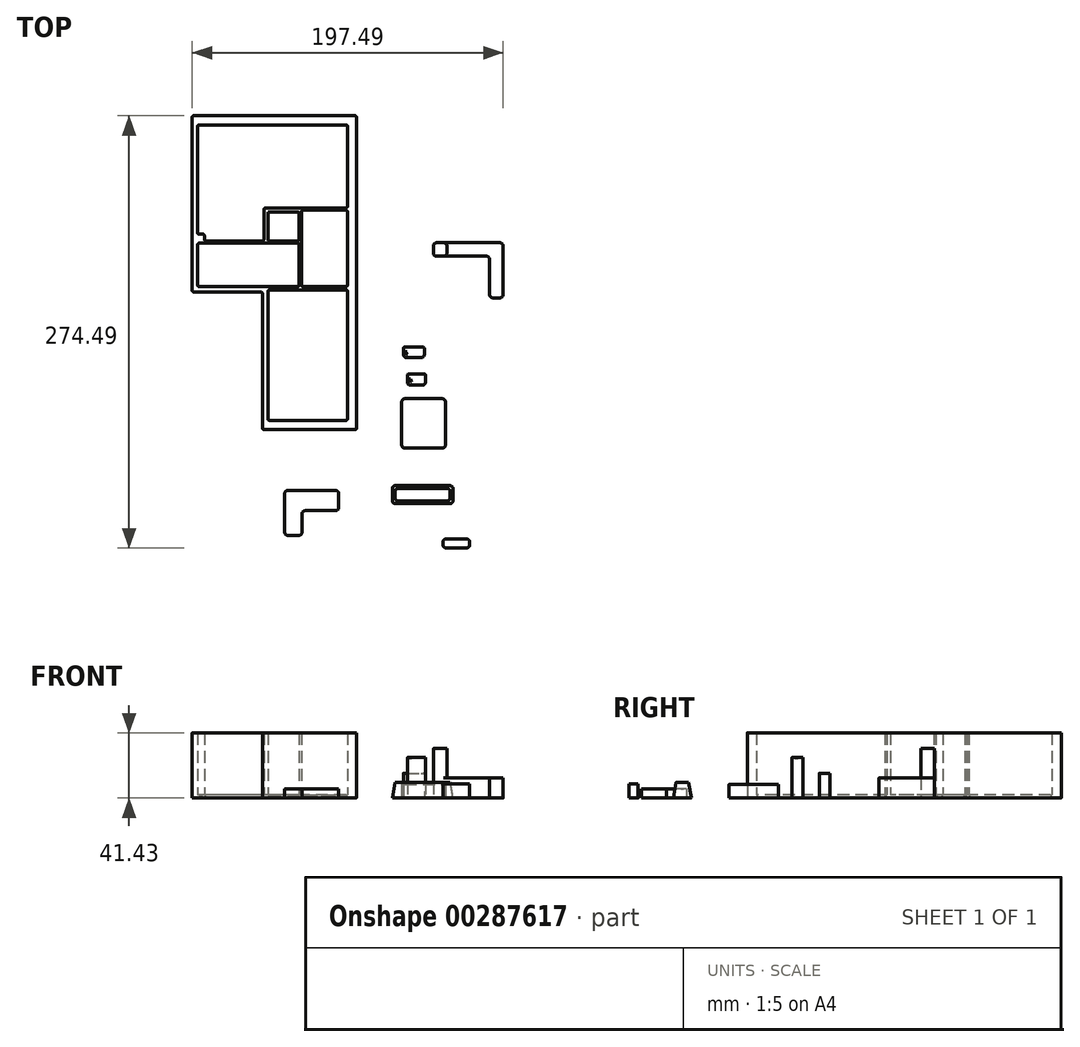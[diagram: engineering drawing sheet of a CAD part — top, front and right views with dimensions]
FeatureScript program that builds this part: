
annotation { "Feature Type Name" : "Feature", "Feature Type Description" : "" }
export const myFeature = defineFeature(function(context is Context, id is Id, definition is map)
    precondition{}
    {
        {
            assignVariable(context, id + "F0", {"name" : "Scale", "anyValue" : 1 / 7});
        }
        {
            var Q0;
            Q0=qCreatedBy(makeId("Top.planeOp"),FACE);
            var sketch = newSketch(context, id + "F1", { "sketchPlane" : qUnion([Q0])});
            skLineSegment(sketch, "E0", {"start": v(0, 0) * mm, "end": v(-59.71, 0) * mm});
            skLineSegment(sketch, "E1", {"start": v(-59.71, 0) * mm, "end": v(-59.71, 87.43) * mm});
            skLineSegment(sketch, "E2", {"start": v(0, 199.36) * mm, "end": v(-104.36, 199.36) * mm});
            skLineSegment(sketch, "E3", {"start": v(0, 0) * mm, "end": v(0, 199.36) * mm});
            skLineSegment(sketch, "E4", {"start": v(-104.36, 199.36) * mm, "end": v(-104.36, 87.43) * mm});
            skLineSegment(sketch, "E5", {"start": v(-104.36, 87.43) * mm, "end": v(-59.71, 87.43) * mm});
            skLineSegment(sketch, "E6", {"start": v(-5.71, 199.36) * mm, "end": v(-5.71, 0) * mm});
            skLineSegment(sketch, "E7", {"start": v(0, 193.5) * mm, "end": v(-104.36, 193.5) * mm});
            skLineSegment(sketch, "E8", {"start": v(-100.93, 199.36) * mm, "end": v(-100.93, 87.43) * mm});
            skLineSegment(sketch, "E9", {"start": v(-56.29, 0) * mm, "end": v(-56.29, 90.86) * mm});
            skLineSegment(sketch, "E10", {"start": v(-56.29, 90.86) * mm, "end": v(-104.36, 90.86) * mm});
            skLineSegment(sketch, "E11", {"start": v(-59.71, 5.86) * mm, "end": v(0, 5.86) * mm});
            skLineSegment(sketch, "E12", {"start": v(-56.29, 90.86) * mm, "end": v(-5.71, 90.86) * mm});
            skLineSegment(sketch, "E13", {"start": v(-34.97, 90.86) * mm, "end": v(-34.97, 139.36) * mm});
            skLineSegment(sketch, "E14", {"start": v(-34.97, 139.36) * mm, "end": v(-5.71, 139.36) * mm});
            skLineSegment(sketch, "E15", {"start": v(-5.71, 140.79) * mm, "end": v(-36.4, 140.79) * mm});
            skLineSegment(sketch, "E16", {"start": v(-36.4, 140.79) * mm, "end": v(-36.4, 90.86) * mm});
            skLineSegment(sketch, "E17", {"start": v(-36.4, 138.29) * mm, "end": v(-56.3, 138.29) * mm});
            skLineSegment(sketch, "E18", {"start": v(-36.4, 140.79) * mm, "end": v(-58.8, 140.79) * mm});
            skLineSegment(sketch, "E19", {"start": v(-58.8, 140.79) * mm, "end": v(-58.8, 119.87) * mm});
            skLineSegment(sketch, "E20", {"start": v(-58.8, 119.87) * mm, "end": v(-36.4, 119.87) * mm});
            skLineSegment(sketch, "E21", {"start": v(-56.3, 138.29) * mm, "end": v(-56.3, 119.87) * mm});
            skLineSegment(sketch, "E22", {"start": v(-36.4, 118.44) * mm, "end": v(-58.8, 118.44) * mm});
            skLineSegment(sketch, "E23", {"start": v(-58.8, 118.44) * mm, "end": v(-58.8, 119.87) * mm});
            skLineSegment(sketch, "E24", {"start": v(-5.71, 88.71) * mm, "end": v(-56.29, 88.71) * mm});
            skLineSegment(sketch, "E25", {"start": v(-56.29, 88.71) * mm, "end": v(-56.29, 90.86) * mm});
            skLineSegment(sketch, "E26", {"start": v(-58.8, 118.44) * mm, "end": v(-100.93, 118.44) * mm});
            skLineSegment(sketch, "E27", {"start": v(-58.8, 119.87) * mm, "end": v(-100.93, 119.87) * mm});
            skLineSegment(sketch, "E28", {"start": v(-100.93, 124.16) * mm, "end": v(-96.64, 124.16) * mm});
            skLineSegment(sketch, "E29", {"start": v(-96.64, 124.16) * mm, "end": v(-96.64, 119.87) * mm});
            skSolve(sketch);
        }
        {
            var Q0;
            Q0 = qSketchRegion(id + "F1", true);
            var Q1;
            {var subQ1=sQuery(id+"F1.wireOp",EDGE,"E17");Q1=makeQuery(id+"F1.imprint","IMPRINT",FACE,{"disambiguationData":[TD([[makeQuery(id+"F1.imprint","IMPRINT",EDGE,{"derivedFrom":subQ1}),-1.0]])]});}
            var Q2;
            {var subQ0=sQuery(id+"F1.wireOp",EDGE,"E13");Q2=makeQuery(id+"F1.imprint","IMPRINT",FACE,{"disambiguationData":[TD([[makeQuery(id+"F1.imprint","IMPRINT",EDGE,{"derivedFrom":subQ0}),1.0]])]});}
            var Q3;
            {var subQ6=sQuery(id+"F1.wireOp",EDGE,"E24");Q3=makeQuery(id+"F1.imprint","IMPRINT",FACE,{"disambiguationData":[TD([[makeQuery(id+"F1.imprint","IMPRINT",EDGE,{"derivedFrom":subQ6}),-1.0]])]});}
            var Q4;
            {var subQ0=sQuery(id+"F1.wireOp",EDGE,"E22");Q4=makeQuery(id+"F1.imprint","IMPRINT",FACE,{"disambiguationData":[TD([[makeQuery(id+"F1.imprint","IMPRINT",EDGE,{"derivedFrom":subQ0}),-1.0]])]});}
            var Q5;
            {var subQ3=sQuery(id+"F1.wireOp",EDGE,"E28");Q5=makeQuery(id+"F1.imprint","IMPRINT",FACE,{"disambiguationData":[TD([[makeQuery(id+"F1.imprint","IMPRINT",EDGE,{"derivedFrom":subQ3}),-1.0]])]});}
            var Q6;
            {var subQ1=sQuery(id+"F1.wireOp",EDGE,"E23");Q6=makeQuery(id+"F1.imprint","IMPRINT",FACE,{"disambiguationData":[TD([[makeQuery(id+"F1.imprint","IMPRINT",EDGE,{"derivedFrom":subQ1}),1.0]])]});}
            extrude(context, id + "F2", {"entities" : qUnion([Q0, Q1, Q2, Q3, Q4, Q5, Q6]), "depth" : (290 * getVariable(context, 'Scale')) * mm});
        }
        {
            var Q0;
            Q0 = qSketchRegion(id + "F1", true);
            var Q1;
            {var subQ0=sQuery(id+"F1.wireOp",EDGE,"E15");Q1=makeQuery(id+"F1.imprint","IMPRINT",FACE,{"disambiguationData":[TD([[makeQuery(id+"F1.imprint","IMPRINT",EDGE,{"derivedFrom":subQ0}),-1.0]])]});}
            var Q2;
            {var subQ1=sQuery(id+"F1.wireOp",EDGE,"E17");Q2=makeQuery(id+"F1.imprint","IMPRINT",FACE,{"disambiguationData":[TD([[makeQuery(id+"F1.imprint","IMPRINT",EDGE,{"derivedFrom":subQ1}),-1.0]])]});}
            var Q3;
            {var subQ4=sQuery(id+"F1.wireOp",EDGE,"E13");Q3=makeQuery(id+"F1.imprint","IMPRINT",FACE,{"disambiguationData":[TD([[makeQuery(id+"F1.imprint","IMPRINT",EDGE,{"derivedFrom":subQ4}),-1.0]])]});}
            var Q4;
            {var subQ3=sQuery(id+"F1.wireOp",EDGE,"E22");Q4=makeQuery(id+"F1.imprint","IMPRINT",FACE,{"disambiguationData":[TD([[makeQuery(id+"F1.imprint","IMPRINT",EDGE,{"derivedFrom":subQ3}),1.0]])]});}
            var Q5;
            {var subQ0=sQuery(id+"F1.wireOp",EDGE,"E17");Q5=makeQuery(id+"F1.imprint","IMPRINT",FACE,{"disambiguationData":[TD([[makeQuery(id+"F1.imprint","IMPRINT",EDGE,{"derivedFrom":subQ0}),1.0]])]});}
            var Q6;
            {var subQ0=sQuery(id+"F1.wireOp",EDGE,"E24");Q6=makeQuery(id+"F1.imprint","IMPRINT",FACE,{"disambiguationData":[TD([[makeQuery(id+"F1.imprint","IMPRINT",EDGE,{"derivedFrom":subQ0}),1.0]])]});}
            var Q7;
            {var subQ6=sQuery(id+"F1.wireOp",EDGE,"E24");Q7=makeQuery(id+"F1.imprint","IMPRINT",FACE,{"disambiguationData":[TD([[makeQuery(id+"F1.imprint","IMPRINT",EDGE,{"derivedFrom":subQ6}),-1.0]])]});}
            var Q8;
            {var subQ0=sQuery(id+"F1.wireOp",EDGE,"E13");Q8=makeQuery(id+"F1.imprint","IMPRINT",FACE,{"disambiguationData":[TD([[makeQuery(id+"F1.imprint","IMPRINT",EDGE,{"derivedFrom":subQ0}),1.0]])]});}
            var Q9;
            {var subQ0=sQuery(id+"F1.wireOp",EDGE,"E22");Q9=makeQuery(id+"F1.imprint","IMPRINT",FACE,{"disambiguationData":[TD([[makeQuery(id+"F1.imprint","IMPRINT",EDGE,{"derivedFrom":subQ0}),-1.0]])]});}
            var Q10;
            {var subQ1=sQuery(id+"F1.wireOp",EDGE,"E23");Q10=makeQuery(id+"F1.imprint","IMPRINT",FACE,{"disambiguationData":[TD([[makeQuery(id+"F1.imprint","IMPRINT",EDGE,{"derivedFrom":subQ1}),1.0]])]});}
            var Q11;
            {var subQ3=sQuery(id+"F1.wireOp",EDGE,"E28");Q11=makeQuery(id+"F1.imprint","IMPRINT",FACE,{"disambiguationData":[TD([[makeQuery(id+"F1.imprint","IMPRINT",EDGE,{"derivedFrom":subQ3}),-1.0]])]});}
            extrude(context, id + "F3", {"entities" : qUnion([Q0, Q1, Q2, Q3, Q4, Q5, Q6, Q7, Q8, Q9, Q10, Q11]), "operationType" : NewBodyOperationType.ADD, "depth" : 2 * mm});
        }
        {
            var Q0;
            Q0=makeQuery(id+"F2.opExtrude","SWEPT_EDGE",EDGE,{"disambiguationData":[OSD([sQuery(id+"F1.wireOp",EDGE,"E7"),sQuery(id+"F1.wireOp",EDGE,"E8")])]});
            var Q1;
            Q1=makeQuery(id+"F2.opExtrude","SWEPT_EDGE",EDGE,{"disambiguationData":[OSD([sQuery(id+"F1.wireOp",EDGE,"E8"),sQuery(id+"F1.wireOp",EDGE,"E28")])]});
            var Q2;
            Q2=makeQuery(id+"F2.opExtrude","SWEPT_EDGE",EDGE,{"disambiguationData":[OSD([sQuery(id+"F1.wireOp",EDGE,"E28"),sQuery(id+"F1.wireOp",EDGE,"E29")])]});
            var Q3;
            Q3=makeQuery(id+"F2.opExtrude","SWEPT_EDGE",EDGE,{"disambiguationData":[OSD([sQuery(id+"F1.wireOp",EDGE,"E27"),sQuery(id+"F1.wireOp",EDGE,"E29")])]});
            var Q4;
            Q4=makeQuery(id+"F2.opExtrude","SWEPT_EDGE",EDGE,{"disambiguationData":[OSD([sQuery(id+"F1.wireOp",EDGE,"E19"),sQuery(id+"F1.wireOp",EDGE,"E20"),sQuery(id+"F1.wireOp",EDGE,"E23"),sQuery(id+"F1.wireOp",EDGE,"E27")])]});
            var Q5;
            Q5=makeQuery(id+"F2.opExtrude","SWEPT_EDGE",EDGE,{"disambiguationData":[OSD([sQuery(id+"F1.wireOp",EDGE,"E18"),sQuery(id+"F1.wireOp",EDGE,"E19")])]});
            var Q6;
            Q6=makeQuery(id+"F2.opExtrude","SWEPT_EDGE",EDGE,{"disambiguationData":[OSD([sQuery(id+"F1.wireOp",EDGE,"E6"),sQuery(id+"F1.wireOp",EDGE,"E15")])]});
            var Q7;
            Q7=makeQuery(id+"F2.opExtrude","SWEPT_EDGE",EDGE,{"disambiguationData":[OSD([sQuery(id+"F1.wireOp",EDGE,"E6"),sQuery(id+"F1.wireOp",EDGE,"E7")])]});
            var Q8;
            Q8=makeQuery(id+"F2.opExtrude","SWEPT_EDGE",EDGE,{"disambiguationData":[OSD([sQuery(id+"F1.wireOp",EDGE,"E16"),sQuery(id+"F1.wireOp",EDGE,"E17")])]});
            var Q9;
            Q9=makeQuery(id+"F2.opExtrude","SWEPT_EDGE",EDGE,{"disambiguationData":[OSD([sQuery(id+"F1.wireOp",EDGE,"E20"),sQuery(id+"F1.wireOp",EDGE,"E21")])]});
            var Q10;
            Q10=makeQuery(id+"F2.opExtrude","SWEPT_EDGE",EDGE,{"disambiguationData":[OSD([sQuery(id+"F1.wireOp",EDGE,"E16"),sQuery(id+"F1.wireOp",EDGE,"E20")])]});
            var Q11;
            Q11=makeQuery(id+"F2.opExtrude","SWEPT_EDGE",EDGE,{"disambiguationData":[OSD([sQuery(id+"F1.wireOp",EDGE,"E13"),sQuery(id+"F1.wireOp",EDGE,"E14")])]});
            var Q12;
            Q12=makeQuery(id+"F2.opExtrude","SWEPT_EDGE",EDGE,{"disambiguationData":[OSD([sQuery(id+"F1.wireOp",EDGE,"E6"),sQuery(id+"F1.wireOp",EDGE,"E12")])]});
            var Q13;
            Q13=makeQuery(id+"F2.opExtrude","SWEPT_EDGE",EDGE,{"disambiguationData":[OSD([sQuery(id+"F1.wireOp",EDGE,"E12"),sQuery(id+"F1.wireOp",EDGE,"E13")])]});
            var Q14;
            Q14=makeQuery(id+"F2.opExtrude","SWEPT_EDGE",EDGE,{"disambiguationData":[OSD([sQuery(id+"F1.wireOp",EDGE,"E16"),sQuery(id+"F1.wireOp",EDGE,"E22")])]});
            var Q15;
            Q15=makeQuery(id+"F2.opExtrude","SWEPT_EDGE",EDGE,{"disambiguationData":[OSD([sQuery(id+"F1.wireOp",EDGE,"E8"),sQuery(id+"F1.wireOp",EDGE,"E10")])]});
            var Q16;
            Q16=makeQuery(id+"F2.opExtrude","SWEPT_EDGE",EDGE,{"disambiguationData":[OSD([sQuery(id+"F1.wireOp",EDGE,"E12"),sQuery(id+"F1.wireOp",EDGE,"E16")])]});
            var Q17;
            Q17=makeQuery(id+"F2.opExtrude","SWEPT_EDGE",EDGE,{"disambiguationData":[OSD([sQuery(id+"F1.wireOp",EDGE,"E6"),sQuery(id+"F1.wireOp",EDGE,"E24")])]});
            var Q18;
            Q18=makeQuery(id+"F2.opExtrude","SWEPT_EDGE",EDGE,{"disambiguationData":[OSD([sQuery(id+"F1.wireOp",EDGE,"E9"),sQuery(id+"F1.wireOp",EDGE,"E24"),sQuery(id+"F1.wireOp",EDGE,"E25")])]});
            var Q19;
            Q19=makeQuery(id+"F2.opExtrude","SWEPT_EDGE",EDGE,{"disambiguationData":[OSD([sQuery(id+"F1.wireOp",EDGE,"E9"),sQuery(id+"F1.wireOp",EDGE,"E11")])]});
            var Q20;
            Q20=makeQuery(id+"F2.opExtrude","SWEPT_EDGE",EDGE,{"disambiguationData":[OSD([sQuery(id+"F1.wireOp",EDGE,"E6"),sQuery(id+"F1.wireOp",EDGE,"E11")])]});
            var Q21;
            Q21=makeQuery(id+"F2.opExtrude","SWEPT_EDGE",EDGE,{"disambiguationData":[OSD([sQuery(id+"F1.wireOp",EDGE,"E6"),sQuery(id+"F1.wireOp",EDGE,"E14")])]});
            var Q22;
            Q22=makeQuery(id+"F2.opExtrude","SWEPT_EDGE",EDGE,{"disambiguationData":[OSD([sQuery(id+"F1.wireOp",EDGE,"E8"),sQuery(id+"F1.wireOp",EDGE,"E26")])]});
            fillet(context, id + "F4", {"entities" : qUnion([Q0, Q1, Q2, Q3, Q4, Q5, Q6, Q7, Q8, Q9, Q10, Q11, Q12, Q13, Q14, Q15, Q16, Q17, Q18, Q19, Q20, Q21, Q22]), "radius" : 1 * mm, "tangentPropagation" : true, "allowEdgeOverflow" : false});
        }
        {
            var Q0;
            Q0=makeQuery(id+"F2.opExtrude","SWEPT_EDGE",EDGE,{"disambiguationData":[OSD([sQuery(id+"F1.wireOp",EDGE,"E0"),sQuery(id+"F1.wireOp",EDGE,"E3")])]});
            var Q1;
            Q1=makeQuery(id+"F2.opExtrude","SWEPT_EDGE",EDGE,{"disambiguationData":[OSD([sQuery(id+"F1.wireOp",EDGE,"E0"),sQuery(id+"F1.wireOp",EDGE,"E1")])]});
            var Q2;
            Q2=makeQuery(id+"F2.opExtrude","SWEPT_EDGE",EDGE,{"disambiguationData":[OSD([sQuery(id+"F1.wireOp",EDGE,"E1"),sQuery(id+"F1.wireOp",EDGE,"E5")])]});
            var Q3;
            Q3=makeQuery(id+"F2.opExtrude","SWEPT_EDGE",EDGE,{"disambiguationData":[OSD([sQuery(id+"F1.wireOp",EDGE,"E4"),sQuery(id+"F1.wireOp",EDGE,"E5")])]});
            var Q4;
            Q4=makeQuery(id+"F2.opExtrude","SWEPT_EDGE",EDGE,{"disambiguationData":[OSD([sQuery(id+"F1.wireOp",EDGE,"E2"),sQuery(id+"F1.wireOp",EDGE,"E4")])]});
            var Q5;
            Q5=makeQuery(id+"F2.opExtrude","SWEPT_EDGE",EDGE,{"disambiguationData":[OSD([sQuery(id+"F1.wireOp",EDGE,"E2"),sQuery(id+"F1.wireOp",EDGE,"E3")])]});
            fillet(context, id + "F5", {"entities" : qUnion([Q0, Q1, Q2, Q3, Q4, Q5]), "radius" : 1 * mm, "tangentPropagation" : true, "allowEdgeOverflow" : false});
        }
        {
            var Q0;
            Q0=qCreatedBy(makeId("Top.planeOp"),FACE);
            var sketch = newSketch(context, id + "F6", { "sketchPlane" : qUnion([Q0])});
            skLineSegment(sketch, "E30.bottom", {"start": v(29.81, 52.55) * mm, "end": v(43.1, 52.55) * mm});
            skLineSegment(sketch, "E30.top", {"start": v(29.81, 45.69) * mm, "end": v(43.1, 45.69) * mm});
            skLineSegment(sketch, "E30.left", {"start": v(29.81, 52.55) * mm, "end": v(29.81, 45.69) * mm});
            skLineSegment(sketch, "E30.right", {"start": v(43.1, 52.55) * mm, "end": v(43.1, 45.69) * mm});
            skSolve(sketch);
        }
        {
            var Q0;
            Q0 = qSketchRegion(id + "F6", true);
            extrude(context, id + "F7", {"entities" : qUnion([Q0]), "depth" : (110 * getVariable(context, 'Scale')) * mm});
        }
        {
            var Q0;
            Q0=makeQuery(id+"F7.opExtrude","SWEPT_EDGE",EDGE,{"disambiguationData":[OSD([sQuery(id+"F6.wireOp",EDGE,"E30.top"),sQuery(id+"F6.wireOp",EDGE,"E30.left")])]});
            var Q1;
            Q1=makeQuery(id+"F7.opExtrude","SWEPT_EDGE",EDGE,{"disambiguationData":[OSD([sQuery(id+"F6.wireOp",EDGE,"E30.top"),sQuery(id+"F6.wireOp",EDGE,"E30.right")])]});
            fillet(context, id + "F8", {"entities" : qUnion([Q0, Q1]), "radius" : 2 * mm, "tangentPropagation" : true, "allowEdgeOverflow" : false});
        }
        {
            var Q0;
            Q0=makeQuery(id+"F7.opExtrude","SWEPT_EDGE",EDGE,{"disambiguationData":[OSD([sQuery(id+"F6.wireOp",EDGE,"E30.bottom"),sQuery(id+"F6.wireOp",EDGE,"E30.right")])]});
            var Q1;
            Q1=makeQuery(id+"F7.opExtrude","SWEPT_EDGE",EDGE,{"disambiguationData":[OSD([sQuery(id+"F6.wireOp",EDGE,"E30.bottom"),sQuery(id+"F6.wireOp",EDGE,"E30.left")])]});
            fillet(context, id + "F9", {"entities" : qUnion([Q0, Q1]), "radius" : 1 * mm, "tangentPropagation" : true, "allowEdgeOverflow" : false});
        }
        {
            var Q0;
            Q0=makeQuery(id+"F7.opExtrude","CAP_FACE",FACE,{"disambiguationData":[OSD([sQuery(id+"F6.wireOp",EDGE,"E30.bottom"),sQuery(id+"F6.wireOp",EDGE,"E30.top"),sQuery(id+"F6.wireOp",EDGE,"E30.left"),sQuery(id+"F6.wireOp",EDGE,"E30.right")])],"isStart":false});
            var sketch = newSketch(context, id + "F10", { "sketchPlane" : qUnion([Q0])});
            skText(sketch, "E31", { "text": "K", "fontName": "OpenSans-Bold.ttf"});
            skPoint(sketch, "E31.firstSnap0", {"position": v(29.81, 49.62) * mm});
            const initialGuessF10  = {"E31": [0.03043, 0.04764, 1, 0, 0.00198]};
            skSetInitialGuess(sketch, initialGuessF10);
            skSolve(sketch);
        }
        {
            var Q0;
            Q0 = qSketchRegion(id + "F10", true);
            extrude(context, id + "F11", {"entities" : qUnion([Q0]), "operationType" : NewBodyOperationType.REMOVE, "oppositeDirection" : true, "depth" : 0.4 * mm});
        }
        {
            var Q0;
            Q0=qCreatedBy(makeId("Top.planeOp"),FACE);
            var sketch = newSketch(context, id + "F12", { "sketchPlane" : qUnion([Q0])});
            skLineSegment(sketch, "E32.bottom", {"start": v(32.25, 35.39) * mm, "end": v(43.83, 35.39) * mm});
            skLineSegment(sketch, "E32.top", {"start": v(32.25, 28.24) * mm, "end": v(43.83, 28.24) * mm});
            skLineSegment(sketch, "E32.left", {"start": v(32.25, 35.39) * mm, "end": v(32.25, 28.24) * mm});
            skLineSegment(sketch, "E32.right", {"start": v(43.83, 35.39) * mm, "end": v(43.83, 28.24) * mm});
            skSolve(sketch);
        }
        {
            var Q0;
            Q0 = qSketchRegion(id + "F12", true);
            extrude(context, id + "F13", {"entities" : qUnion([Q0]), "depth" : (180 * getVariable(context, 'Scale')) * mm});
        }
        {
            var Q0;
            Q0=makeQuery(id+"F13.opExtrude","SWEPT_EDGE",EDGE,{"disambiguationData":[OSD([sQuery(id+"F12.wireOp",EDGE,"E32.top"),sQuery(id+"F12.wireOp",EDGE,"E32.left")])]});
            var Q1;
            Q1=makeQuery(id+"F13.opExtrude","SWEPT_EDGE",EDGE,{"disambiguationData":[OSD([sQuery(id+"F12.wireOp",EDGE,"E32.top"),sQuery(id+"F12.wireOp",EDGE,"E32.right")])]});
            fillet(context, id + "F14", {"entities" : qUnion([Q0, Q1]), "radius" : 2 * mm, "tangentPropagation" : true, "allowEdgeOverflow" : false});
        }
        {
            var Q0;
            Q0=makeQuery(id+"F13.opExtrude","SWEPT_EDGE",EDGE,{"disambiguationData":[OSD([sQuery(id+"F12.wireOp",EDGE,"E32.bottom"),sQuery(id+"F12.wireOp",EDGE,"E32.right")])]});
            var Q1;
            Q1=makeQuery(id+"F13.opExtrude","SWEPT_EDGE",EDGE,{"disambiguationData":[OSD([sQuery(id+"F12.wireOp",EDGE,"E32.bottom"),sQuery(id+"F12.wireOp",EDGE,"E32.left")])]});
            fillet(context, id + "F15", {"entities" : qUnion([Q0, Q1]), "radius" : 1 * mm, "tangentPropagation" : true, "allowEdgeOverflow" : false});
        }
        {
            var Q0;
            Q0=makeQuery(id+"F13.opExtrude","CAP_FACE",FACE,{"disambiguationData":[OSD([sQuery(id+"F12.wireOp",EDGE,"E32.bottom"),sQuery(id+"F12.wireOp",EDGE,"E32.top"),sQuery(id+"F12.wireOp",EDGE,"E32.left"),sQuery(id+"F12.wireOp",EDGE,"E32.right")])],"isStart":false});
            var sketch = newSketch(context, id + "F16", { "sketchPlane" : qUnion([Q0])});
            skText(sketch, "E33", { "text": "A", "fontName": "OpenSans-Bold.ttf"});
            skPoint(sketch, "E33.firstSnap0", {"position": v(32.25, 32.32) * mm});
            const initialGuessF16  = {"E33": [0.03308, 0.03035, 1, 0, 0.00196]};
            skSetInitialGuess(sketch, initialGuessF16);
            skSolve(sketch);
        }
        {
            var Q0;
            Q0 = qSketchRegion(id + "F16", true);
            extrude(context, id + "F17", {"entities" : qUnion([Q0]), "operationType" : NewBodyOperationType.REMOVE, "oppositeDirection" : true, "depth" : 0.4 * mm});
        }
        {
            var Q0;
            Q0=qCreatedBy(makeId("Top.planeOp"),FACE);
            var sketch = newSketch(context, id + "F18", { "sketchPlane" : qUnion([Q0])});
            skLineSegment(sketch, "E34.bottom", {"start": v(28.75, 19.63) * mm, "end": v(56.47, 19.63) * mm});
            skLineSegment(sketch, "E34.top", {"start": v(28.75, -11.8) * mm, "end": v(56.47, -11.8) * mm});
            skLineSegment(sketch, "E34.left", {"start": v(28.75, 19.63) * mm, "end": v(28.75, -11.8) * mm});
            skLineSegment(sketch, "E34.right", {"start": v(56.47, 19.63) * mm, "end": v(56.47, -11.8) * mm});
            skSolve(sketch);
        }
        {
            var Q0;
            Q0 = qSketchRegion(id + "F18", true);
            extrude(context, id + "F19", {"entities" : qUnion([Q0]), "depth" : (60 * getVariable(context, 'Scale')) * mm});
        }
        {
            var Q0;
            Q0=makeQuery(id+"F19.opExtrude","SWEPT_EDGE",EDGE,{"disambiguationData":[OSD([sQuery(id+"F18.wireOp",EDGE,"E34.top"),sQuery(id+"F18.wireOp",EDGE,"E34.left")])]});
            var Q1;
            Q1=makeQuery(id+"F19.opExtrude","SWEPT_EDGE",EDGE,{"disambiguationData":[OSD([sQuery(id+"F18.wireOp",EDGE,"E34.top"),sQuery(id+"F18.wireOp",EDGE,"E34.right")])]});
            var Q2;
            Q2=makeQuery(id+"F19.opExtrude","SWEPT_EDGE",EDGE,{"disambiguationData":[OSD([sQuery(id+"F18.wireOp",EDGE,"E34.bottom"),sQuery(id+"F18.wireOp",EDGE,"E34.right")])]});
            var Q3;
            Q3=makeQuery(id+"F19.opExtrude","SWEPT_EDGE",EDGE,{"disambiguationData":[OSD([sQuery(id+"F18.wireOp",EDGE,"E34.bottom"),sQuery(id+"F18.wireOp",EDGE,"E34.left")])]});
            fillet(context, id + "F20", {"entities" : qUnion([Q0, Q1, Q2, Q3]), "radius" : 2 * mm, "tangentPropagation" : true, "allowEdgeOverflow" : false});
        }
        {
            var Q0;
            Q0=qCreatedBy(makeId("Top.planeOp"),FACE);
            var sketch = newSketch(context, id + "F21", { "sketchPlane" : qUnion([Q0])});
            skLineSegment(sketch, "E35.bottom", {"start": v(22.73, -35.6) * mm, "end": v(61.3, -35.6) * mm});
            skLineSegment(sketch, "E35.top", {"start": v(22.73, -47.02) * mm, "end": v(61.3, -47.02) * mm});
            skLineSegment(sketch, "E35.left", {"start": v(22.73, -35.6) * mm, "end": v(22.73, -47.02) * mm});
            skLineSegment(sketch, "E35.right", {"start": v(61.3, -35.6) * mm, "end": v(61.3, -47.02) * mm});
            skSolve(sketch);
        }
        {
            var Q0;
            Q0=makeQuery(id+"F21.imprint","IMPRINT",FACE,{"disambiguationData":[TD([[makeQuery(id+"F21.imprint","IMPRINT",EDGE,{"derivedFrom":sQuery(id+"F21.wireOp",EDGE,"E35.bottom")}),-1.0]])]});
            extrude(context, id + "F22", {"entities" : qUnion([Q0]), "depth" : (70 * getVariable(context, 'Scale')) * mm, "hasDraft" : true, "draftAngle" : 10 * degree, "draftPullDirection" : true});
        }
        {
            var Q0;
            Q0=makeQuery(id+"F22.opExtrude","SWEPT_EDGE",EDGE,{"disambiguationData":[OSD([sQuery(id+"F21.wireOp",EDGE,"E35.top"),sQuery(id+"F21.wireOp",EDGE,"E35.right")])]});
            var Q1;
            Q1=makeQuery(id+"F22.opExtrude","SWEPT_EDGE",EDGE,{"disambiguationData":[OSD([sQuery(id+"F21.wireOp",EDGE,"E35.top"),sQuery(id+"F21.wireOp",EDGE,"E35.left")])]});
            var Q2;
            Q2=makeQuery(id+"F22.opExtrude","SWEPT_EDGE",EDGE,{"disambiguationData":[OSD([sQuery(id+"F21.wireOp",EDGE,"E35.bottom"),sQuery(id+"F21.wireOp",EDGE,"E35.right")])]});
            var Q3;
            Q3=makeQuery(id+"F22.opExtrude","SWEPT_EDGE",EDGE,{"disambiguationData":[OSD([sQuery(id+"F21.wireOp",EDGE,"E35.bottom"),sQuery(id+"F21.wireOp",EDGE,"E35.left")])]});
            fillet(context, id + "F23", {"entities" : qUnion([Q0, Q1, Q2, Q3]), "radius" : 2 * mm, "tangentPropagation" : true, "allowEdgeOverflow" : false});
        }
        {
            var Q0;
            Q0=qCreatedBy(makeId("Top.planeOp"),FACE);
            var sketch = newSketch(context, id + "F24", { "sketchPlane" : qUnion([Q0])});
            skLineSegment(sketch, "E36", {"start": v(-45.6, -38.64) * mm, "end": v(-11.3, -38.64) * mm});
            skLineSegment(sketch, "E37", {"start": v(-11.3, -38.64) * mm, "end": v(-11.3, -51.5) * mm});
            skLineSegment(sketch, "E38", {"start": v(-11.3, -51.5) * mm, "end": v(-34.6, -51.5) * mm});
            skLineSegment(sketch, "E39", {"start": v(-34.6, -51.5) * mm, "end": v(-34.6, -67.2) * mm});
            skLineSegment(sketch, "E40", {"start": v(-34.6, -67.2) * mm, "end": v(-45.6, -67.2) * mm});
            skLineSegment(sketch, "E41", {"start": v(-45.6, -67.2) * mm, "end": v(-45.6, -38.64) * mm});
            skSolve(sketch);
        }
        {
            var Q0;
            Q0 = qSketchRegion(id + "F24", true);
            extrude(context, id + "F25", {"entities" : qUnion([Q0]), "depth" : (40 * getVariable(context, 'Scale')) * mm});
        }
        {
            var Q0;
            Q0=makeQuery(id+"F25.opExtrude","SWEPT_EDGE",EDGE,{"disambiguationData":[OSD([sQuery(id+"F24.wireOp",EDGE,"E39"),sQuery(id+"F24.wireOp",EDGE,"E40")])]});
            var Q1;
            Q1=makeQuery(id+"F25.opExtrude","SWEPT_EDGE",EDGE,{"disambiguationData":[OSD([sQuery(id+"F24.wireOp",EDGE,"E40"),sQuery(id+"F24.wireOp",EDGE,"E41")])]});
            var Q2;
            Q2=makeQuery(id+"F25.opExtrude","SWEPT_EDGE",EDGE,{"disambiguationData":[OSD([sQuery(id+"F24.wireOp",EDGE,"E37"),sQuery(id+"F24.wireOp",EDGE,"E38")])]});
            var Q3;
            Q3=makeQuery(id+"F25.opExtrude","SWEPT_EDGE",EDGE,{"disambiguationData":[OSD([sQuery(id+"F24.wireOp",EDGE,"E36"),sQuery(id+"F24.wireOp",EDGE,"E37")])]});
            var Q4;
            Q4=makeQuery(id+"F25.opExtrude","SWEPT_EDGE",EDGE,{"disambiguationData":[OSD([sQuery(id+"F24.wireOp",EDGE,"E36"),sQuery(id+"F24.wireOp",EDGE,"E41")])]});
            var Q5;
            Q5=makeQuery(id+"F25.opExtrude","SWEPT_EDGE",EDGE,{"disambiguationData":[OSD([sQuery(id+"F24.wireOp",EDGE,"E38"),sQuery(id+"F24.wireOp",EDGE,"E39")])]});
            fillet(context, id + "F26", {"entities" : qUnion([Q0, Q1, Q2, Q3, Q4, Q5]), "radius" : 2 * mm, "tangentPropagation" : true, "allowEdgeOverflow" : false});
        }
        {
            var Q0;
            Q0=qCreatedBy(makeId("Top.planeOp"),FACE);
            var sketch = newSketch(context, id + "F27", { "sketchPlane" : qUnion([Q0])});
            skLineSegment(sketch, "E42", {"start": v(48.85, 118.7) * mm, "end": v(93.13, 118.7) * mm});
            skLineSegment(sketch, "E43", {"start": v(93.13, 118.7) * mm, "end": v(93.13, 83.7) * mm});
            skLineSegment(sketch, "E44", {"start": v(93.13, 83.7) * mm, "end": v(84.56, 83.7) * mm});
            skLineSegment(sketch, "E45", {"start": v(84.56, 83.7) * mm, "end": v(84.56, 110.13) * mm});
            skLineSegment(sketch, "E46", {"start": v(84.56, 110.13) * mm, "end": v(48.85, 110.13) * mm});
            skLineSegment(sketch, "E47", {"start": v(48.85, 110.13) * mm, "end": v(48.85, 118.7) * mm});
            skLineSegment(sketch, "E48", {"start": v(57.42, 118.7) * mm, "end": v(57.42, 110.13) * mm});
            skSolve(sketch);
        }
        {
            var Q0;
            {var subQ1=sQuery(id+"F27.wireOp",EDGE,"E43");Q0=makeQuery(id+"F27.imprint","IMPRINT",FACE,{"disambiguationData":[TD([[makeQuery(id+"F27.imprint","IMPRINT",EDGE,{"derivedFrom":subQ1}),-1.0]])]});}
            extrude(context, id + "F28", {"entities" : qUnion([Q0]), "depth" : (90 * getVariable(context, 'Scale')) * mm});
        }
        {
            var Q0;
            {var subQ0=sQuery(id+"F27.wireOp",EDGE,"E47");Q0=makeQuery(id+"F27.imprint","IMPRINT",FACE,{"disambiguationData":[TD([[makeQuery(id+"F27.imprint","IMPRINT",EDGE,{"derivedFrom":subQ0}),-1.0]])]});}
            extrude(context, id + "F29", {"entities" : qUnion([Q0]), "operationType" : NewBodyOperationType.ADD, "depth" : (220 * getVariable(context, 'Scale')) * mm});
        }
        {
            var Q0;
            Q0=makeQuery(id+"F28.opExtrude","SWEPT_EDGE",EDGE,{"disambiguationData":[OSD([sQuery(id+"F27.wireOp",EDGE,"E46"),sQuery(id+"F27.wireOp",EDGE,"E47")])]});
            var Q1;
            Q1=makeQuery(id+"F28.opExtrude","SWEPT_EDGE",EDGE,{"disambiguationData":[OSD([sQuery(id+"F27.wireOp",EDGE,"E45"),sQuery(id+"F27.wireOp",EDGE,"E46")])]});
            var Q2;
            Q2=makeQuery(id+"F28.opExtrude","SWEPT_EDGE",EDGE,{"disambiguationData":[OSD([sQuery(id+"F27.wireOp",EDGE,"E44"),sQuery(id+"F27.wireOp",EDGE,"E45")])]});
            var Q3;
            Q3=makeQuery(id+"F28.opExtrude","SWEPT_EDGE",EDGE,{"disambiguationData":[OSD([sQuery(id+"F27.wireOp",EDGE,"E43"),sQuery(id+"F27.wireOp",EDGE,"E44")])]});
            var Q4;
            Q4=makeQuery(id+"F28.opExtrude","SWEPT_EDGE",EDGE,{"disambiguationData":[OSD([sQuery(id+"F27.wireOp",EDGE,"E42"),sQuery(id+"F27.wireOp",EDGE,"E43")])]});
            var Q5;
            Q5=makeQuery(id+"F28.opExtrude","SWEPT_EDGE",EDGE,{"disambiguationData":[OSD([sQuery(id+"F27.wireOp",EDGE,"E42"),sQuery(id+"F27.wireOp",EDGE,"E47")])]});
            var Q6;
            Q6=makeQuery(id+"F29.opExtrude","SWEPT_EDGE",EDGE,{"disambiguationData":[OSD([sQuery(id+"F27.wireOp",EDGE,"E46"),sQuery(id+"F27.wireOp",EDGE,"E48")])]});
            var Q7;
            Q7=makeQuery(id+"F29.opExtrude","SWEPT_EDGE",EDGE,{"disambiguationData":[OSD([sQuery(id+"F27.wireOp",EDGE,"E42"),sQuery(id+"F27.wireOp",EDGE,"E48")])]});
            var Q8;
            Q8=makeQuery(id+"F29.opExtrude","SWEPT_EDGE",EDGE,{"disambiguationData":[OSD([sQuery(id+"F27.wireOp",EDGE,"E46"),sQuery(id+"F27.wireOp",EDGE,"E47")])]});
            var Q9;
            Q9=makeQuery(id+"F29.opExtrude","SWEPT_EDGE",EDGE,{"disambiguationData":[OSD([sQuery(id+"F27.wireOp",EDGE,"E42"),sQuery(id+"F27.wireOp",EDGE,"E47")])]});
            fillet(context, id + "F30", {"entities" : qUnion([Q0, Q1, Q2, Q3, Q4, Q5, Q6, Q7, Q8, Q9]), "radius" : 2 * mm, "tangentPropagation" : true, "allowEdgeOverflow" : false});
        }
        {
            var Q0;
            Q0=qCreatedBy(makeId("Top.planeOp"),FACE);
            var sketch = newSketch(context, id + "F31", { "sketchPlane" : qUnion([Q0])});
            skLineSegment(sketch, "E49.bottom", {"start": v(54.9, -69.41) * mm, "end": v(71.9, -69.41) * mm});
            skLineSegment(sketch, "E49.top", {"start": v(54.9, -75.13) * mm, "end": v(71.9, -75.13) * mm});
            skLineSegment(sketch, "E49.left", {"start": v(54.9, -69.41) * mm, "end": v(54.9, -75.13) * mm});
            skLineSegment(sketch, "E49.right", {"start": v(71.9, -69.41) * mm, "end": v(71.9, -75.13) * mm});
            skSolve(sketch);
        }
        {
            var Q0;
            Q0=makeQuery(id+"F31.imprint","IMPRINT",FACE,{"disambiguationData":[TD([[makeQuery(id+"F31.imprint","IMPRINT",EDGE,{"derivedFrom":sQuery(id+"F31.wireOp",EDGE,"E49.bottom")}),-1.0]])]});
            extrude(context, id + "F32", {"entities" : qUnion([Q0]), "depth" : (63 * getVariable(context, 'Scale')) * mm});
        }
        {
            var Q0;
            Q0=makeQuery(id+"F32.opExtrude","SWEPT_EDGE",EDGE,{"disambiguationData":[OSD([sQuery(id+"F31.wireOp",EDGE,"E49.top"),sQuery(id+"F31.wireOp",EDGE,"E49.right")])]});
            var Q1;
            Q1=makeQuery(id+"F32.opExtrude","SWEPT_EDGE",EDGE,{"disambiguationData":[OSD([sQuery(id+"F31.wireOp",EDGE,"E49.top"),sQuery(id+"F31.wireOp",EDGE,"E49.left")])]});
            var Q2;
            Q2=makeQuery(id+"F32.opExtrude","SWEPT_EDGE",EDGE,{"disambiguationData":[OSD([sQuery(id+"F31.wireOp",EDGE,"E49.bottom"),sQuery(id+"F31.wireOp",EDGE,"E49.right")])]});
            var Q3;
            Q3=makeQuery(id+"F32.opExtrude","SWEPT_EDGE",EDGE,{"disambiguationData":[OSD([sQuery(id+"F31.wireOp",EDGE,"E49.bottom"),sQuery(id+"F31.wireOp",EDGE,"E49.left")])]});
            fillet(context, id + "F33", {"entities" : qUnion([Q0, Q1, Q2, Q3]), "radius" : 2 * mm, "tangentPropagation" : true, "allowEdgeOverflow" : false});
        }
    });
